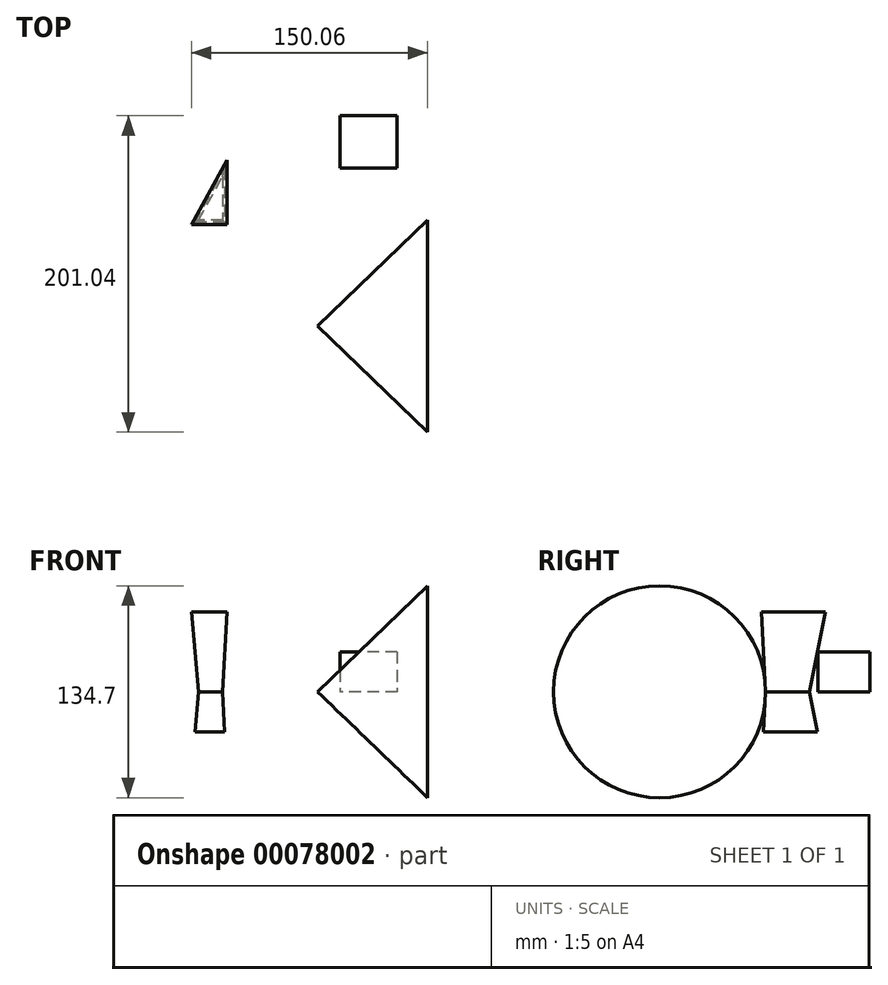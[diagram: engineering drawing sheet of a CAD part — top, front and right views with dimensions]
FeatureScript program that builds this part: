
annotation { "Feature Type Name" : "Feature", "Feature Type Description" : "" }
export const myFeature = defineFeature(function(context is Context, id is Id, definition is map)
    precondition{}
    {
        {
            var Q0;
            Q0=qCreatedBy(makeId("Top.planeOp"),FACE);
            var sketch = newSketch(context, id + "F0", { "sketchPlane" : qUnion([Q0])});
            skLineSegment(sketch, "E0", {"start": v(-75.7, 0) * mm, "end": v(-60.3, 27.77) * mm});
            skLineSegment(sketch, "E1", {"start": v(-60.3, 27.77) * mm, "end": v(-60.3, 0) * mm});
            skLineSegment(sketch, "E2", {"start": v(-60.3, 0) * mm, "end": v(-75.7, 0) * mm});
            skSolve(sketch);
        }
        {
            var Q0;
            Q0=makeQuery(id+"F0.imprint","IMPRINT",FACE,{"disambiguationData":[TD([[makeQuery(id+"F0.imprint","IMPRINT",EDGE,{"derivedFrom":sQuery(id+"F0.wireOp",EDGE,"E0")}),-1.0]])]});
            extrude(context, id + "F1", {"entities" : qUnion([Q0]), "depth" : 50.8 * mm, "hasDraft" : true, "draftAngle" : 3 * degree, "hasSecondDirection" : true, "secondDirectionOppositeDirection" : true, "secondDirectionDepth" : 25.4 * mm, "hasSecondDirectionDraft" : true, "secondDirectionDraftAngle" : 3 * degree});
        }
        {
            var Q0;
            Q0=qCreatedBy(makeId("Top.planeOp"),FACE);
            var sketch = newSketch(context, id + "F2", { "sketchPlane" : qUnion([Q0])});
            skLineSegment(sketch, "E3", {"start": v(0, -67.35) * mm, "end": v(69.84, -67.35) * mm});
            skLineSegment(sketch, "E4", {"start": v(69.84, -67.35) * mm, "end": v(69.84, 0) * mm});
            skLineSegment(sketch, "E5", {"start": v(0, -67.35) * mm, "end": v(69.84, 0) * mm});
            skSolve(sketch);
        }
        {
            var Q0;
            Q0=makeQuery(id+"F2.imprint","IMPRINT",FACE,{"disambiguationData":[TD([[makeQuery(id+"F2.imprint","IMPRINT",EDGE,{"derivedFrom":sQuery(id+"F2.wireOp",EDGE,"E3")}),1.0]])]});
            var Q1;
            Q1=sQuery(id+"F2.wireOp",EDGE,"E3");
            revolve(context, id + "F3", {"entities" : qUnion([Q0]), "axis" : qUnion([Q1]), "revolveType" : RevolveType.FULL});
        }
        {
            var Q0;
            Q0=qCreatedBy(makeId("Top.planeOp"),FACE);
            var sketch = newSketch(context, id + "F4", { "sketchPlane" : qUnion([Q0])});
            skLineSegment(sketch, "E6.bottom", {"start": v(50.55, 66.35) * mm, "end": v(14.32, 66.35) * mm});
            skLineSegment(sketch, "E6.top", {"start": v(50.55, 33.16) * mm, "end": v(14.32, 33.16) * mm});
            skLineSegment(sketch, "E6.left", {"start": v(50.55, 66.35) * mm, "end": v(50.55, 33.16) * mm});
            skLineSegment(sketch, "E6.right", {"start": v(14.32, 66.35) * mm, "end": v(14.32, 33.16) * mm});
            skSolve(sketch);
        }
        {
            var Q0;
            Q0 = qSketchRegion(id + "F4", true);
            extrude(context, id + "F6", {"entities" : qUnion([Q0]), "depth" : 25.4 * mm});
        }
    });
